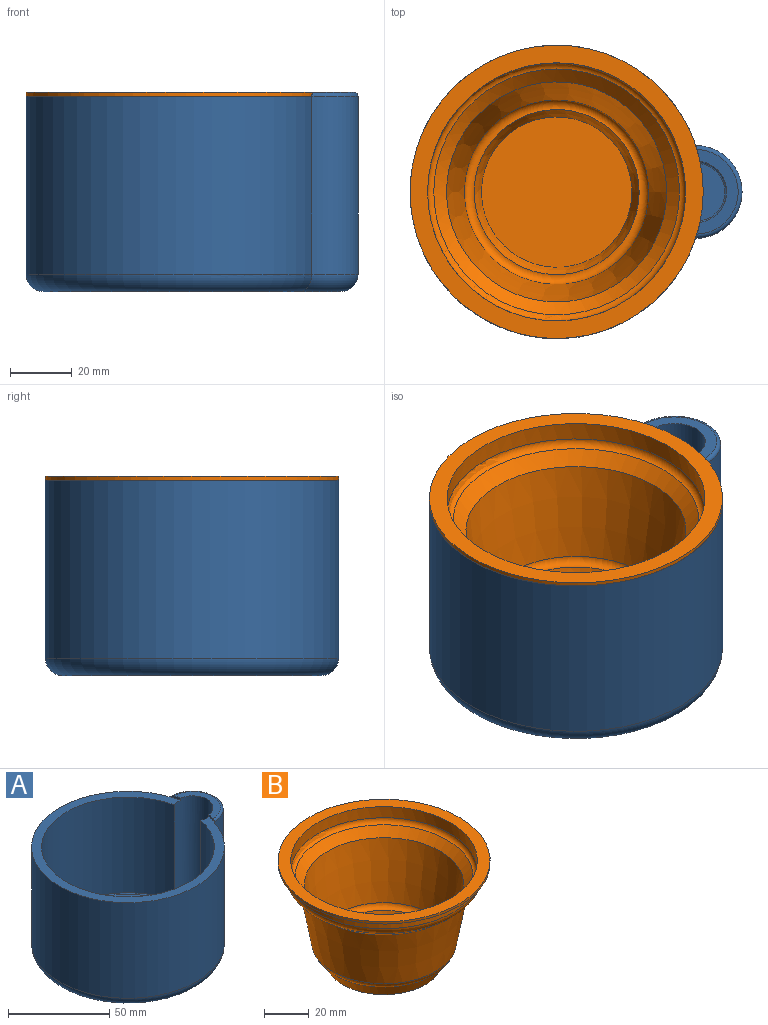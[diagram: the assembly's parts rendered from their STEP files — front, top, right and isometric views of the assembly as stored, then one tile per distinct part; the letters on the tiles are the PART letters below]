
ASSEMBLY  parts=2 mates=1
PART A: 15 faces, bbox 113x103.1x64.6 mm
  f0: plane 95.25x94.21mm, normal (0,0,1), area 1318.6mm2, adj f1,f6,f7,f11,f12
  f1: cylinder r=47.62mm len=95.25mm, axis (0,0,-1), area 15527.8mm2, adj f0,f2,f5
  f2: cylinder r=15mm len=57.79mm, axis (0,0,-1), area 2723.1mm2, adj f1,f4,f14
  f3: plane 96.65x84.07mm, normal (0,0,-1), area 5754.3mm2, adj f4,f5
  f4: torus R=9.41mm, axis (0,0,1), area 383.7mm2, adj f2,f3,f5
  f5: torus R=42.04mm, axis (0,0,1), area 2286.8mm2, adj f1,f3,f4
  f6: cylinder r=42.62mm len=85.25mm, axis (0,0,-1), area 14389.4mm2, adj f0,f7,f10
  f7: cylinder r=10mm len=59.06mm, axis (0,0,-1), area 2278.5mm2, adj f0,f6,f9,f11,f12,f13
  f8: plane 96.65x84.07mm, normal (0,0,1), area 5754.3mm2, adj f9,f10
  f9: torus R=9.41mm, axis (0,0,1), area 35.7mm2, adj f7,f8,f10
  f10: torus R=42.04mm, axis (0,0,1), area 229.5mm2, adj f6,f8,f9
  f11: cylinder r=47.62mm len=5.1mm, axis (0,0,-1), area 6.3mm2, adj f0,f7,f13,f14
  f12: cylinder r=47.62mm len=5.1mm, axis (0,0,-1), area 6.3mm2, adj f0,f7,f13,f14
  f13: plane 27.45x13.33mm, normal (0,0,1), area 132.2mm2, adj f7,f11,f12,f14
  f14: torus R=13.73mm, axis (0,0,1), area 90.3mm2, adj f2,f11,f12,f13
PART B: 17 faces, bbox 96.2x96.2x55.2 mm
  f0: plane 52.38x52.38mm, normal (0,0,-1), area 2154.4mm2, adj f1
  f1: cone r=28.57mm half-angle=20.6deg, axis (0,0,1), area 1167.1mm2, adj f0,f9
  f2: cone r=38.1mm half-angle=10.3deg, axis (0,0,1), area 6958.1mm2, adj f3,f9
  f3: cone r=41.27mm half-angle=45deg, axis (0,0,1), area 1119.7mm2, adj f2,f8
  f4: cylinder r=44.45mm len=88.9mm, axis (0,0,-1), area 1345mm2, adj f7,f8
  f5: cylinder r=47.62mm len=95.25mm, axis (0,0,-1), area 380mm2, adj f6,f7
  f6: plane 95.25x95.25mm, normal (0,0,1), area 1607.5mm2, adj f5,f10
  f7: plane 95.25x95.25mm, normal (0,0,-1), area 918.4mm2, adj f4,f5
  f8: torus R=39.37mm, axis (0,0,-1), area 1641.2mm2, adj f3,f4
  f9: torus R=27.49mm, axis (0,0,-1), area 1160.8mm2, adj f1,f2
  f10: cylinder r=41.91mm len=83.82mm, axis (0,0,-1), area 1602.5mm2, adj f6,f15
  f11: plane 48.86x48.86mm, normal (0,0,1), area 1874.8mm2, adj f12
  f12: cone r=26.2mm half-angle=20.6deg, axis (0,0,1), area 1087.8mm2, adj f11,f16
  f13: cone r=35.6mm half-angle=10.3deg, axis (0,0,1), area 6643.3mm2, adj f14,f16
  f14: cone r=39.48mm half-angle=45deg, axis (0,0,1), area 1400.7mm2, adj f13,f15
  f15: torus R=39.37mm, axis (0,0,-1), area 891.9mm2, adj f10,f14
  f16: torus R=27.49mm, axis (0,0,-1), area 761.2mm2, adj f12,f13
PLACE A at identity
PLACE B t=(0,0,9.4)mm
MATE planar B.f4 <-> A.f1  axis (0,0,-1) through (0,0,63.37)mm
